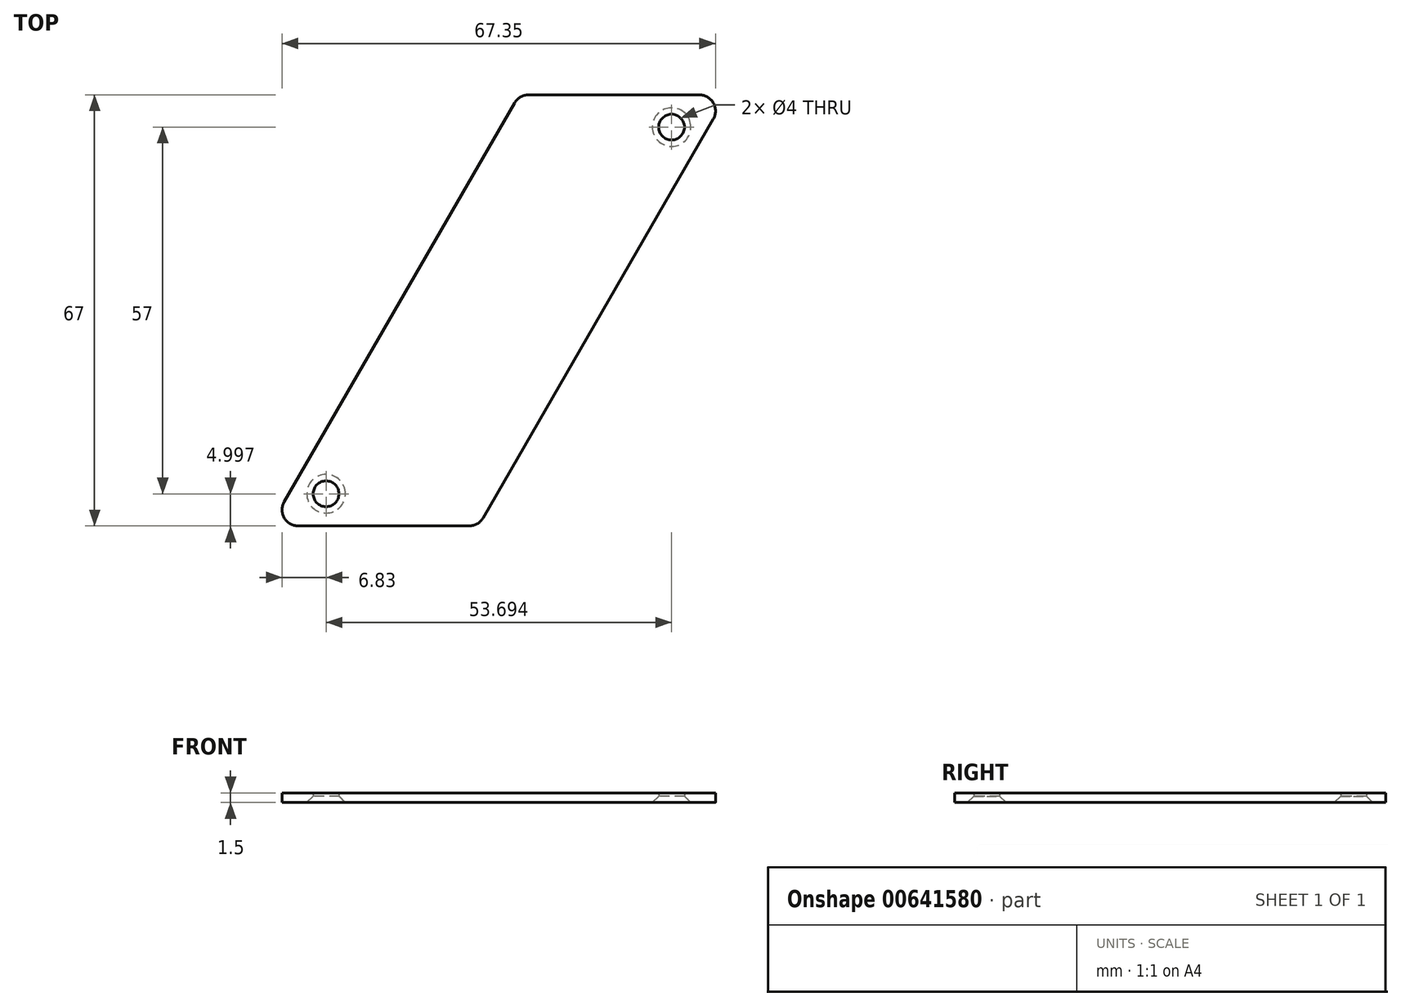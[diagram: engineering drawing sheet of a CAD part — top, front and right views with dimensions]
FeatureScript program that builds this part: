
annotation { "Feature Type Name" : "Feature", "Feature Type Description" : "" }
export const myFeature = defineFeature(function(context is Context, id is Id, definition is map)
    precondition{}
    {
        {
            var Q0;
            Q0=qCreatedBy(makeId("Top.planeOp"),FACE);
            var sketch = newSketch(context, id + "F0", { "sketchPlane" : qUnion([Q0])});
            skLineSegment(sketch, "E0", {"start": v(-44.99, -34.27) * mm, "end": v(-9.19, 27.73) * mm});
            skLineSegment(sketch, "E1", {"start": v(-7.02, 28.98) * mm, "end": v(19.53, 28.98) * mm});
            skLineSegment(sketch, "E2", {"start": v(21.7, 25.23) * mm, "end": v(-14.1, -36.77) * mm});
            skLineSegment(sketch, "E3", {"start": v(-16.26, -38.02) * mm, "end": v(-42.82, -38.02) * mm});
            skPoint(sketch, "E4.visualSharp", {"position": v(23.86, 28.98) * mm});
            skArc(sketch, "E4.filletArc", {"start": v(21.7, 25.23) * mm, "mid": v(21.7, 27.73) * mm, "end": v(19.53, 28.98) * mm});
            skPoint(sketch, "E5.visualSharp", {"position": v(-8.47, 28.98) * mm});
            skArc(sketch, "E5.filletArc", {"start": v(-7.02, 28.98) * mm, "mid": v(-8.27, 28.64) * mm, "end": v(-9.19, 27.73) * mm});
            skPoint(sketch, "E6.visualSharp", {"position": v(-14.82, -38.02) * mm});
            skArc(sketch, "E6.filletArc", {"start": v(-16.26, -38.02) * mm, "mid": v(-15.01, -37.69) * mm, "end": v(-14.1, -36.77) * mm});
            skPoint(sketch, "E7.visualSharp", {"position": v(-47.15, -38.02) * mm});
            skArc(sketch, "E7.filletArc", {"start": v(-44.99, -34.27) * mm, "mid": v(-44.99, -36.77) * mm, "end": v(-42.82, -38.02) * mm});
            skCircle(sketch, "E8", {"center": v(-38.49, -33.02) * mm, "radius": 2 * mm});
            skCircle(sketch, "E9", {"center": v(15.2, 23.98) * mm, "radius": 2 * mm});
            skSolve(sketch);
        }
        {
            var Q0;
            Q0=makeQuery(id+"F0.imprint","IMPRINT",FACE,{"disambiguationData":[TD([[makeQuery(id+"F0.imprint","IMPRINT",EDGE,{"derivedFrom":sQuery(id+"F0.wireOp",EDGE,"E0")}),-1.0]])]});
            extrude(context, id + "F1", {"entities" : qUnion([Q0]), "depth" : 1.5 * mm, "offsetDistance" : 25 * mm});
        }
        {
            var Q0;
            Q0=makeQuery(id+"F1.opExtrude","CAP_EDGE",EDGE,{"disambiguationData":[OSD([sQuery(id+"F0.wireOp",EDGE,"E9")])],"isStart":true});
            var Q1;
            Q1=makeQuery(id+"F1.opExtrude","CAP_EDGE",EDGE,{"disambiguationData":[OSD([sQuery(id+"F0.wireOp",EDGE,"E8")])],"isStart":true});
            chamfer(context, id + "F2", {"entities" : qUnion([Q0, Q1]), "width" : 1 * mm, "tangentPropagation" : true});
        }
    });
